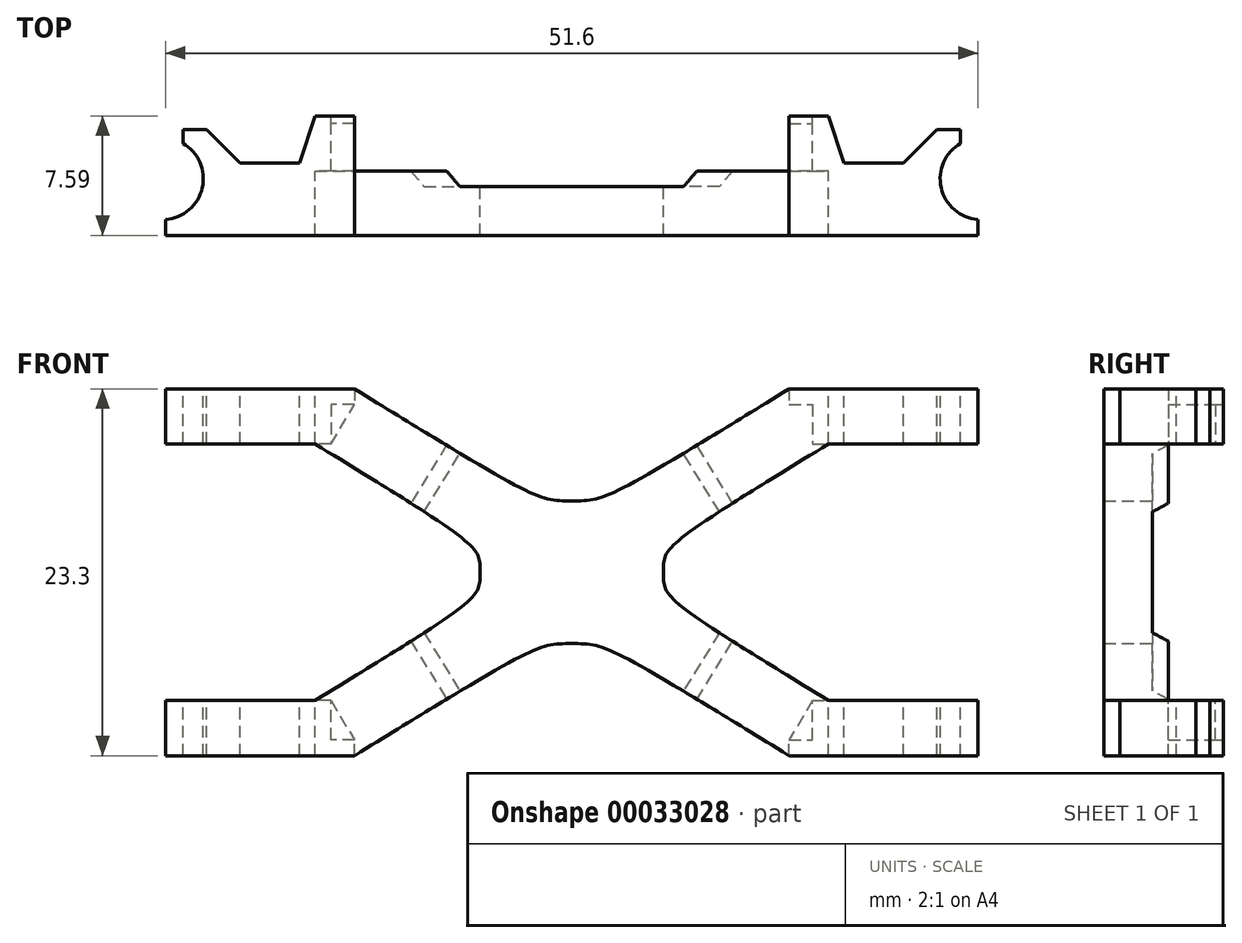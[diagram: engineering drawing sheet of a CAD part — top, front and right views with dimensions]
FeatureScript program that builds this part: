
annotation { "Feature Type Name" : "Feature", "Feature Type Description" : "" }
export const myFeature = defineFeature(function(context is Context, id is Id, definition is map)
    precondition{}
    {
        {
            var Q0;
            Q0=qCreatedBy(makeId("Front.planeOp"),FACE);
            var sketch = newSketch(context, id + "F0", { "sketchPlane" : qUnion([Q0])});
            skLineSegment(sketch, "E0", {"start": v(-15.3, 10.65) * mm, "end": v(-15.3, 8.15) * mm});
            skLineSegment(sketch, "E1", {"start": v(-15.3, 8.15) * mm, "end": v(-16.3, 8.15) * mm});
            skLineSegment(sketch, "E2", {"start": v(-16.3, 8.15) * mm, "end": v(-16.3, 11.65) * mm});
            skLineSegment(sketch, "E3", {"start": v(-16.3, 11.65) * mm, "end": v(-13.8, 11.65) * mm});
            skLineSegment(sketch, "E4", {"start": v(-13.8, 11.65) * mm, "end": v(-13.8, 10.65) * mm});
            skLineSegment(sketch, "E5", {"start": v(-13.8, 10.65) * mm, "end": v(-15.3, 10.65) * mm});
            skLineSegment(sketch, "E6.MirrorCS", {"start": v(13.8, 10.65) * mm, "end": v(15.3, 10.65) * mm});
            skLineSegment(sketch, "E7.MirrorCS", {"start": v(13.8, 11.65) * mm, "end": v(13.8, 10.65) * mm});
            skLineSegment(sketch, "E8.MirrorCS", {"start": v(16.3, 11.65) * mm, "end": v(13.8, 11.65) * mm});
            skLineSegment(sketch, "E9.MirrorCS", {"start": v(16.3, 8.15) * mm, "end": v(16.3, 11.65) * mm});
            skLineSegment(sketch, "E10.MirrorCS", {"start": v(15.3, 10.65) * mm, "end": v(15.3, 8.15) * mm});
            skLineSegment(sketch, "E11.MirrorCS", {"start": v(15.3, 8.15) * mm, "end": v(16.3, 8.15) * mm});
            skLineSegment(sketch, "E12.MirrorCS", {"start": v(15.3, -8.15) * mm, "end": v(16.3, -8.15) * mm});
            skLineSegment(sketch, "E13.MirrorCS", {"start": v(15.3, -10.65) * mm, "end": v(15.3, -8.15) * mm});
            skLineSegment(sketch, "E14.MirrorCS", {"start": v(13.8, -11.65) * mm, "end": v(13.8, -10.65) * mm});
            skLineSegment(sketch, "E15.MirrorCS", {"start": v(16.3, -11.65) * mm, "end": v(13.8, -11.65) * mm});
            skLineSegment(sketch, "E16.MirrorCS", {"start": v(16.3, -8.15) * mm, "end": v(16.3, -11.65) * mm});
            skLineSegment(sketch, "E17.MirrorCS", {"start": v(13.8, -10.65) * mm, "end": v(15.3, -10.65) * mm});
            skLineSegment(sketch, "E18.MirrorCS", {"start": v(-13.8, -11.65) * mm, "end": v(-13.8, -10.65) * mm});
            skLineSegment(sketch, "E19.MirrorCS", {"start": v(-13.8, -10.65) * mm, "end": v(-15.3, -10.65) * mm});
            skLineSegment(sketch, "E20.MirrorCS", {"start": v(-16.3, -11.65) * mm, "end": v(-13.8, -11.65) * mm});
            skLineSegment(sketch, "E21.MirrorCS", {"start": v(-16.3, -8.15) * mm, "end": v(-16.3, -11.65) * mm});
            skLineSegment(sketch, "E22.MirrorCS", {"start": v(-15.3, -8.15) * mm, "end": v(-16.3, -8.15) * mm});
            skLineSegment(sketch, "E23.MirrorCS", {"start": v(-15.3, -10.65) * mm, "end": v(-15.3, -8.15) * mm});
            skSolve(sketch);
        }
        {
            var Q0;
            Q0=qCreatedBy(makeId("Front.planeOp"),FACE);
            var sketch = newSketch(context, id + "F1", { "sketchPlane" : qUnion([Q0])});
            skPoint(sketch, "E24.0", {"position": v(-13.8, 11.65) * mm});
            skPoint(sketch, "E25.0", {"position": v(-16.3, 8.15) * mm});
            skFitSpline(sketch, "E26", {"points": [v(-13.8, 11.65) * mm, v(0, 4.53) * mm], "startDerivative": vector(34.73, -21.35) * mm, "endDerivative": vector(6.67, 0) * mm});
            skFitSpline(sketch, "E27", {"points": [v(-16.3, 8.15) * mm, v(-5.81, 0) * mm], "startDerivative": vector(31.46, -19.34) * mm, "endDerivative": vector(0, -5.11) * mm});
            skFitSpline(sketch, "E28.MirrorCS", {"points": [v(13.8, 11.65) * mm, v(0, 4.53) * mm], "startDerivative": vector(-34.73, -21.35) * mm, "endDerivative": vector(-6.67, 0) * mm});
            skFitSpline(sketch, "E29.MirrorCS", {"points": [v(16.3, 8.15) * mm, v(5.81, 0) * mm], "startDerivative": vector(-31.46, -19.34) * mm, "endDerivative": vector(0, -5.11) * mm});
            skFitSpline(sketch, "E30.MirrorCS", {"points": [v(-16.3, -8.15) * mm, v(-5.81, 0) * mm], "startDerivative": vector(31.46, 19.34) * mm, "endDerivative": vector(0, 5.11) * mm});
            skFitSpline(sketch, "E31.MirrorCS", {"points": [v(-13.8, -11.65) * mm, v(0, -4.53) * mm], "startDerivative": vector(34.73, 21.35) * mm, "endDerivative": vector(6.67, 0) * mm});
            skFitSpline(sketch, "E32.MirrorCS", {"points": [v(13.8, -11.65) * mm, v(0, -4.53) * mm], "startDerivative": vector(-34.73, 21.35) * mm, "endDerivative": vector(-6.67, 0) * mm});
            skFitSpline(sketch, "E33.MirrorCS", {"points": [v(16.3, -8.15) * mm, v(5.81, 0) * mm], "startDerivative": vector(-31.46, 19.34) * mm, "endDerivative": vector(0, 5.11) * mm});
            skLineSegment(sketch, "E34", {"start": v(-13.8, 11.65) * mm, "end": v(-27.96, 11.65) * mm});
            skLineSegment(sketch, "E35", {"start": v(-27.96, 11.65) * mm, "end": v(-27.96, 8.15) * mm});
            skLineSegment(sketch, "E36", {"start": v(-27.96, 8.15) * mm, "end": v(-16.3, 8.15) * mm});
            skLineSegment(sketch, "E37.MirrorCS", {"start": v(27.96, 11.65) * mm, "end": v(27.96, 8.15) * mm});
            skLineSegment(sketch, "E38.MirrorCS", {"start": v(27.96, 8.15) * mm, "end": v(16.3, 8.15) * mm});
            skLineSegment(sketch, "E39.MirrorCS", {"start": v(13.8, 11.65) * mm, "end": v(27.96, 11.65) * mm});
            skLineSegment(sketch, "E40.MirrorCS", {"start": v(27.96, -8.15) * mm, "end": v(16.3, -8.15) * mm});
            skLineSegment(sketch, "E41.MirrorCS", {"start": v(27.96, -11.65) * mm, "end": v(27.96, -8.15) * mm});
            skLineSegment(sketch, "E42.MirrorCS", {"start": v(13.8, -11.65) * mm, "end": v(27.96, -11.65) * mm});
            skLineSegment(sketch, "E43.MirrorCS", {"start": v(-27.96, -8.15) * mm, "end": v(-16.3, -8.15) * mm});
            skLineSegment(sketch, "E44.MirrorCS", {"start": v(-13.8, -11.65) * mm, "end": v(-27.96, -11.65) * mm});
            skLineSegment(sketch, "E45.MirrorCS", {"start": v(-27.96, -11.65) * mm, "end": v(-27.96, -8.15) * mm});
            skLineSegment(sketch, "E46.0", {"start": v(-13.8, -11.65) * mm, "end": v(-13.8, -10.65) * mm});
            skLineSegment(sketch, "E47.0", {"start": v(-13.8, -10.65) * mm, "end": v(-15.3, -10.65) * mm});
            skLineSegment(sketch, "E48.0", {"start": v(-15.3, -10.65) * mm, "end": v(-15.3, -8.15) * mm});
            skLineSegment(sketch, "E49.0", {"start": v(-15.3, -8.15) * mm, "end": v(-16.3, -8.15) * mm});
            skLineSegment(sketch, "E50.0", {"start": v(13.8, -11.65) * mm, "end": v(13.8, -10.65) * mm});
            skLineSegment(sketch, "E51.0", {"start": v(13.8, -10.65) * mm, "end": v(15.3, -10.65) * mm});
            skLineSegment(sketch, "E52.0", {"start": v(15.3, -10.65) * mm, "end": v(15.3, -8.15) * mm});
            skLineSegment(sketch, "E53.0", {"start": v(15.3, -8.15) * mm, "end": v(16.3, -8.15) * mm});
            skLineSegment(sketch, "E54.0", {"start": v(15.3, 8.15) * mm, "end": v(16.3, 8.15) * mm});
            skLineSegment(sketch, "E55.0", {"start": v(15.3, 10.65) * mm, "end": v(15.3, 8.15) * mm});
            skLineSegment(sketch, "E56.0", {"start": v(13.8, 10.65) * mm, "end": v(15.3, 10.65) * mm});
            skLineSegment(sketch, "E57.0", {"start": v(13.8, 11.65) * mm, "end": v(13.8, 10.65) * mm});
            skLineSegment(sketch, "E58.0", {"start": v(-13.8, 11.65) * mm, "end": v(-13.8, 10.65) * mm});
            skLineSegment(sketch, "E59.0", {"start": v(-13.8, 10.65) * mm, "end": v(-15.3, 10.65) * mm});
            skLineSegment(sketch, "E60.0", {"start": v(-15.3, 10.65) * mm, "end": v(-15.3, 8.15) * mm});
            skLineSegment(sketch, "E61.0", {"start": v(-15.3, 8.15) * mm, "end": v(-16.3, 8.15) * mm});
            skLineSegment(sketch, "E62", {"start": v(-15.3, 8.15) * mm, "end": v(-13.8, 10.65) * mm});
            skLineSegment(sketch, "E63", {"start": v(13.8, 10.65) * mm, "end": v(15.3, 8.15) * mm});
            skLineSegment(sketch, "E64", {"start": v(15.3, -8.15) * mm, "end": v(13.8, -10.65) * mm});
            skLineSegment(sketch, "E65", {"start": v(-15.3, -8.15) * mm, "end": v(-13.8, -10.65) * mm});
            skLineSegment(sketch, "E66", {"start": v(-13.8, 11.65) * mm, "end": v(-2.22, 4.53) * mm, "construction": true});
            skLineSegment(sketch, "E67", {"start": v(-5.81, 1.7) * mm, "end": v(-16.3, 8.15) * mm, "construction": true});
            skLineSegment(sketch, "E68", {"start": v(-9.37, 3.85) * mm, "end": v(-7.1, 7.55) * mm});
            skLineSegment(sketch, "E69.MirrorCS", {"start": v(9.37, 3.85) * mm, "end": v(7.1, 7.55) * mm});
            skLineSegment(sketch, "E70.MirrorCS", {"start": v(-9.37, -3.85) * mm, "end": v(-7.1, -7.55) * mm});
            skLineSegment(sketch, "E71.MirrorCS", {"start": v(9.37, -3.85) * mm, "end": v(7.1, -7.55) * mm});
            skSolve(sketch);
        }
        {
            var Q0;
            Q0=qCreatedBy(makeId("Top.planeOp"),FACE);
            var sketch = newSketch(context, id + "F2", { "sketchPlane" : qUnion([Q0])});
            skCircle(sketch, "E72", {"center": v(-26, -4) * mm, "radius": 2.5 * mm, "construction": true});
            skLineSegment(sketch, "E73", {"start": v(0, 0) * mm, "end": v(-16.3, 0) * mm});
            skArc(sketch, "E74", {"start": v(-25.8, -6.6) * mm, "mid": v(-23.46, -4.58) * mm, "end": v(-24.7, -1.75) * mm});
            skLineSegment(sketch, "E75", {"start": v(-25.8, -7.6) * mm, "end": v(-25.8, -6.6) * mm});
            skLineSegment(sketch, "E76", {"start": v(-24.7, -1.75) * mm, "end": v(-22.46, -3.04) * mm, "construction": true});
            skLineSegment(sketch, "E77", {"start": v(-24.7, -0.87) * mm, "end": v(-24.7, -1.75) * mm});
            skLineSegment(sketch, "E78", {"start": v(-25.8, -7.6) * mm, "end": v(0, -7.6) * mm});
            skLineSegment(sketch, "E79.MirrorCS", {"start": v(0, 0) * mm, "end": v(16.3, 0) * mm});
            skLineSegment(sketch, "E80.MirrorCS", {"start": v(25.8, -7.6) * mm, "end": v(0, -7.6) * mm});
            skLineSegment(sketch, "E81.MirrorCS", {"start": v(25.8, -7.6) * mm, "end": v(25.8, -6.6) * mm});
            skArc(sketch, "E82.MirrorCS", {"start": v(25.8, -6.6) * mm, "mid": v(23.46, -4.58) * mm, "end": v(24.7, -1.75) * mm});
            skLineSegment(sketch, "E83.MirrorCS", {"start": v(24.7, -0.87) * mm, "end": v(24.7, -1.75) * mm});
            skPoint(sketch, "E84.0", {"position": v(-16.3, 0) * mm});
            skLineSegment(sketch, "E85", {"start": v(-24.7, -0.87) * mm, "end": v(-23.2, -0.87) * mm});
            skLineSegment(sketch, "E86", {"start": v(-17.3, -3) * mm, "end": v(-16.3, 0) * mm});
            skPoint(sketch, "E87.orphan", {"position": v(-24.7, 0) * mm});
            skLineSegment(sketch, "E88.MirrorCS", {"start": v(24.7, -0.87) * mm, "end": v(23.2, -0.87) * mm});
            skLineSegment(sketch, "E89.MirrorCS", {"start": v(17.3, -3) * mm, "end": v(16.3, 0) * mm});
            skPoint(sketch, "E90.orphan", {"position": v(24.7, 0) * mm});
            skLineSegment(sketch, "E91", {"start": v(-23.2, -0.87) * mm, "end": v(-21.07, -3) * mm});
            skLineSegment(sketch, "E92", {"start": v(-21.07, -3) * mm, "end": v(-17.3, -3) * mm});
            skLineSegment(sketch, "E93.MirrorCS", {"start": v(23.2, -0.87) * mm, "end": v(21.07, -3) * mm});
            skLineSegment(sketch, "E94.MirrorCS", {"start": v(21.07, -3) * mm, "end": v(17.3, -3) * mm});
            skSolve(sketch);
        }
        {
            var Q0;
            Q0=makeQuery(id+"F1.imprint","IMPRINT",FACE,{"disambiguationData":[TD([[makeQuery(id+"F1.imprint","IMPRINT",EDGE,{"derivedFrom":sQuery(id+"F1.wireOp",EDGE,"E34")}),1.0]])]});
            var Q1;
            Q1=makeQuery(id+"F1.imprint","IMPRINT",FACE,{"disambiguationData":[TD([[makeQuery(id+"F1.imprint","IMPRINT",EDGE,{"derivedFrom":sQuery(id+"F1.wireOp",EDGE,"E59.0")}),1.0]])]});
            var Q2;
            {var subQ2=sQuery(id+"F1.wireOp",EDGE,"E58.0");Q2=makeQuery(id+"F1.imprint","IMPRINT",FACE,{"disambiguationData":[TD([[makeQuery(id+"F1.imprint","IMPRINT",EDGE,{"derivedFrom":subQ2}),1.0]])]});}
            var Q3;
            {var subQ2=sQuery(id+"F1.wireOp",EDGE,"E68");Q3=makeQuery(id+"F1.imprint","IMPRINT",FACE,{"disambiguationData":[TD([[makeQuery(id+"F1.imprint","IMPRINT",EDGE,{"derivedFrom":subQ2}),-1.0]])]});}
            var Q4;
            {var subQ2=sQuery(id+"F1.wireOp",EDGE,"E46.0");Q4=makeQuery(id+"F1.imprint","IMPRINT",FACE,{"disambiguationData":[TD([[makeQuery(id+"F1.imprint","IMPRINT",EDGE,{"derivedFrom":subQ2}),-1.0]])]});}
            var Q5;
            Q5=makeQuery(id+"F1.imprint","IMPRINT",FACE,{"disambiguationData":[TD([[makeQuery(id+"F1.imprint","IMPRINT",EDGE,{"derivedFrom":sQuery(id+"F1.wireOp",EDGE,"E47.0")}),-1.0]])]});
            var Q6;
            Q6=makeQuery(id+"F1.imprint","IMPRINT",FACE,{"disambiguationData":[TD([[makeQuery(id+"F1.imprint","IMPRINT",EDGE,{"derivedFrom":sQuery(id+"F1.wireOp",EDGE,"E43.MirrorCS")}),-1.0]])]});
            var Q7;
            {var subQ2=sQuery(id+"F1.wireOp",EDGE,"E50.0");Q7=makeQuery(id+"F1.imprint","IMPRINT",FACE,{"disambiguationData":[TD([[makeQuery(id+"F1.imprint","IMPRINT",EDGE,{"derivedFrom":subQ2}),1.0]])]});}
            var Q8;
            Q8=makeQuery(id+"F1.imprint","IMPRINT",FACE,{"disambiguationData":[TD([[makeQuery(id+"F1.imprint","IMPRINT",EDGE,{"derivedFrom":sQuery(id+"F1.wireOp",EDGE,"E51.0")}),1.0]])]});
            var Q9;
            Q9=makeQuery(id+"F1.imprint","IMPRINT",FACE,{"disambiguationData":[TD([[makeQuery(id+"F1.imprint","IMPRINT",EDGE,{"derivedFrom":sQuery(id+"F1.wireOp",EDGE,"E40.MirrorCS")}),1.0]])]});
            var Q10;
            {var subQ1=sQuery(id+"F1.wireOp",EDGE,"E54.0");Q10=makeQuery(id+"F1.imprint","IMPRINT",FACE,{"disambiguationData":[TD([[makeQuery(id+"F1.imprint","IMPRINT",EDGE,{"derivedFrom":subQ1}),-1.0]])]});}
            var Q11;
            Q11=makeQuery(id+"F1.imprint","IMPRINT",FACE,{"disambiguationData":[TD([[makeQuery(id+"F1.imprint","IMPRINT",EDGE,{"derivedFrom":sQuery(id+"F1.wireOp",EDGE,"E37.MirrorCS")}),-1.0]])]});
            var Q12;
            Q12=makeQuery(id+"F1.imprint","IMPRINT",FACE,{"disambiguationData":[TD([[makeQuery(id+"F1.imprint","IMPRINT",EDGE,{"derivedFrom":sQuery(id+"F1.wireOp",EDGE,"E55.0")}),-1.0]])]});
            extrude(context, id + "F3", {"entities" : qUnion([Q0, Q1, Q2, Q3, Q4, Q5, Q6, Q7, Q8, Q9, Q10, Q11, Q12]), "depth" : 25 * mm});
        }
        {
            var Q0;
            Q0=makeQuery(id+"F2.imprint","IMPRINT",FACE,{"disambiguationData":[TD([[makeQuery(id+"F2.imprint","IMPRINT",EDGE,{"derivedFrom":sQuery(id+"F2.wireOp",EDGE,"E73")}),1.0]])]});
            extrude(context, id + "F4", {"entities" : qUnion([Q0]), "operationType" : NewBodyOperationType.INTERSECT, "endBound" : BoundingType.SYMMETRIC, "oppositeDirection" : true, "depth" : 30 * mm});
        }
        {
            var Q0;
            Q0=makeQuery(id+"F1.imprint","IMPRINT",FACE,{"disambiguationData":[TD([[makeQuery(id+"F1.imprint","IMPRINT",EDGE,{"derivedFrom":sQuery(id+"F1.wireOp",EDGE,"E26")}),-1.0]])]});
            var Q1;
            {var subQ2=sQuery(id+"F1.wireOp",EDGE,"E68");Q1=makeQuery(id+"F1.imprint","IMPRINT",FACE,{"disambiguationData":[TD([[makeQuery(id+"F1.imprint","IMPRINT",EDGE,{"derivedFrom":subQ2}),-1.0]])]});}
            var Q2;
            {var subQ2=sQuery(id+"F1.wireOp",EDGE,"E46.0");Q2=makeQuery(id+"F1.imprint","IMPRINT",FACE,{"disambiguationData":[TD([[makeQuery(id+"F1.imprint","IMPRINT",EDGE,{"derivedFrom":subQ2}),-1.0]])]});}
            var Q3;
            {var subQ2=sQuery(id+"F1.wireOp",EDGE,"E50.0");Q3=makeQuery(id+"F1.imprint","IMPRINT",FACE,{"disambiguationData":[TD([[makeQuery(id+"F1.imprint","IMPRINT",EDGE,{"derivedFrom":subQ2}),1.0]])]});}
            var Q4;
            {var subQ1=sQuery(id+"F1.wireOp",EDGE,"E54.0");Q4=makeQuery(id+"F1.imprint","IMPRINT",FACE,{"disambiguationData":[TD([[makeQuery(id+"F1.imprint","IMPRINT",EDGE,{"derivedFrom":subQ1}),-1.0]])]});}
            var Q5;
            Q5=makeQuery(id+"F1.imprint","IMPRINT",FACE,{"disambiguationData":[TD([[makeQuery(id+"F1.imprint","IMPRINT",EDGE,{"derivedFrom":sQuery(id+"F1.wireOp",EDGE,"E59.0")}),1.0]])]});
            var Q6;
            Q6=makeQuery(id+"F1.imprint","IMPRINT",FACE,{"disambiguationData":[TD([[makeQuery(id+"F1.imprint","IMPRINT",EDGE,{"derivedFrom":sQuery(id+"F1.wireOp",EDGE,"E47.0")}),-1.0]])]});
            var Q7;
            Q7=makeQuery(id+"F1.imprint","IMPRINT",FACE,{"disambiguationData":[TD([[makeQuery(id+"F1.imprint","IMPRINT",EDGE,{"derivedFrom":sQuery(id+"F1.wireOp",EDGE,"E51.0")}),1.0]])]});
            var Q8;
            Q8=makeQuery(id+"F1.imprint","IMPRINT",FACE,{"disambiguationData":[TD([[makeQuery(id+"F1.imprint","IMPRINT",EDGE,{"derivedFrom":sQuery(id+"F1.wireOp",EDGE,"E55.0")}),-1.0]])]});
            extrude(context, id + "F5", {"entities" : qUnion([Q0, Q1, Q2, Q3, Q4, Q5, Q6, Q7, Q8]), "operationType" : NewBodyOperationType.REMOVE, "depth" : 3.5 * mm});
        }
        {
            var Q0;
            {var subQ2=sQuery(id+"F1.wireOp",EDGE,"E68");Q0=makeQuery(id+"F1.imprint","IMPRINT",FACE,{"disambiguationData":[TD([[makeQuery(id+"F1.imprint","IMPRINT",EDGE,{"derivedFrom":subQ2}),-1.0]])]});}
            extrude(context, id + "F6", {"entities" : qUnion([Q0]), "operationType" : NewBodyOperationType.REMOVE, "depth" : 4.5 * mm});
        }
        {
            var Q0;
            Q0=makeQuery(id+"F6.boolean.opBoolean","INTERSECT",EDGE,{"derivedFrom":[makeQuery(id+"F5.boolean.opBoolean","COPY",FACE,{"derivedFrom":makeQuery(id+"F5.opExtrude","CAP_FACE",FACE,{"disambiguationData":[OSD([sQuery(id+"F1.wireOp",EDGE,"E26"),sQuery(id+"F1.wireOp",EDGE,"E27"),sQuery(id+"F1.wireOp",EDGE,"E28.MirrorCS"),sQuery(id+"F1.wireOp",EDGE,"E29.MirrorCS"),sQuery(id+"F1.wireOp",EDGE,"E30.MirrorCS"),sQuery(id+"F1.wireOp",EDGE,"E31.MirrorCS"),sQuery(id+"F1.wireOp",EDGE,"E32.MirrorCS"),sQuery(id+"F1.wireOp",EDGE,"E33.MirrorCS"),sQuery(id+"F1.wireOp",EDGE,"E46.0"),sQuery(id+"F1.wireOp",EDGE,"E47.0"),sQuery(id+"F1.wireOp",EDGE,"E48.0"),sQuery(id+"F1.wireOp",EDGE,"E49.0"),sQuery(id+"F1.wireOp",EDGE,"E50.0"),sQuery(id+"F1.wireOp",EDGE,"E51.0"),sQuery(id+"F1.wireOp",EDGE,"E52.0"),sQuery(id+"F1.wireOp",EDGE,"E53.0"),sQuery(id+"F1.wireOp",EDGE,"E54.0"),sQuery(id+"F1.wireOp",EDGE,"E55.0"),sQuery(id+"F1.wireOp",EDGE,"E56.0"),sQuery(id+"F1.wireOp",EDGE,"E57.0"),sQuery(id+"F1.wireOp",EDGE,"E58.0"),sQuery(id+"F1.wireOp",EDGE,"E59.0"),sQuery(id+"F1.wireOp",EDGE,"E60.0"),sQuery(id+"F1.wireOp",EDGE,"E61.0")])],"isStart":false})}),makeQuery(id+"F6.opExtrude","SWEPT_FACE",FACE,{"disambiguationData":[OSD([sQuery(id+"F1.wireOp",EDGE,"E69.MirrorCS")])]})]});
            var Q1;
            Q1=makeQuery(id+"F6.boolean.opBoolean","INTERSECT",EDGE,{"derivedFrom":[makeQuery(id+"F5.boolean.opBoolean","COPY",FACE,{"derivedFrom":makeQuery(id+"F5.opExtrude","CAP_FACE",FACE,{"disambiguationData":[OSD([sQuery(id+"F1.wireOp",EDGE,"E26"),sQuery(id+"F1.wireOp",EDGE,"E27"),sQuery(id+"F1.wireOp",EDGE,"E28.MirrorCS"),sQuery(id+"F1.wireOp",EDGE,"E29.MirrorCS"),sQuery(id+"F1.wireOp",EDGE,"E30.MirrorCS"),sQuery(id+"F1.wireOp",EDGE,"E31.MirrorCS"),sQuery(id+"F1.wireOp",EDGE,"E32.MirrorCS"),sQuery(id+"F1.wireOp",EDGE,"E33.MirrorCS"),sQuery(id+"F1.wireOp",EDGE,"E46.0"),sQuery(id+"F1.wireOp",EDGE,"E47.0"),sQuery(id+"F1.wireOp",EDGE,"E48.0"),sQuery(id+"F1.wireOp",EDGE,"E49.0"),sQuery(id+"F1.wireOp",EDGE,"E50.0"),sQuery(id+"F1.wireOp",EDGE,"E51.0"),sQuery(id+"F1.wireOp",EDGE,"E52.0"),sQuery(id+"F1.wireOp",EDGE,"E53.0"),sQuery(id+"F1.wireOp",EDGE,"E54.0"),sQuery(id+"F1.wireOp",EDGE,"E55.0"),sQuery(id+"F1.wireOp",EDGE,"E56.0"),sQuery(id+"F1.wireOp",EDGE,"E57.0"),sQuery(id+"F1.wireOp",EDGE,"E58.0"),sQuery(id+"F1.wireOp",EDGE,"E59.0"),sQuery(id+"F1.wireOp",EDGE,"E60.0"),sQuery(id+"F1.wireOp",EDGE,"E61.0")])],"isStart":false})}),makeQuery(id+"F6.opExtrude","SWEPT_FACE",FACE,{"disambiguationData":[OSD([sQuery(id+"F1.wireOp",EDGE,"E68")])]})]});
            var Q2;
            Q2=makeQuery(id+"F6.boolean.opBoolean","INTERSECT",EDGE,{"derivedFrom":[makeQuery(id+"F5.boolean.opBoolean","COPY",FACE,{"derivedFrom":makeQuery(id+"F5.opExtrude","CAP_FACE",FACE,{"disambiguationData":[OSD([sQuery(id+"F1.wireOp",EDGE,"E26"),sQuery(id+"F1.wireOp",EDGE,"E27"),sQuery(id+"F1.wireOp",EDGE,"E28.MirrorCS"),sQuery(id+"F1.wireOp",EDGE,"E29.MirrorCS"),sQuery(id+"F1.wireOp",EDGE,"E30.MirrorCS"),sQuery(id+"F1.wireOp",EDGE,"E31.MirrorCS"),sQuery(id+"F1.wireOp",EDGE,"E32.MirrorCS"),sQuery(id+"F1.wireOp",EDGE,"E33.MirrorCS"),sQuery(id+"F1.wireOp",EDGE,"E46.0"),sQuery(id+"F1.wireOp",EDGE,"E47.0"),sQuery(id+"F1.wireOp",EDGE,"E48.0"),sQuery(id+"F1.wireOp",EDGE,"E49.0"),sQuery(id+"F1.wireOp",EDGE,"E50.0"),sQuery(id+"F1.wireOp",EDGE,"E51.0"),sQuery(id+"F1.wireOp",EDGE,"E52.0"),sQuery(id+"F1.wireOp",EDGE,"E53.0"),sQuery(id+"F1.wireOp",EDGE,"E54.0"),sQuery(id+"F1.wireOp",EDGE,"E55.0"),sQuery(id+"F1.wireOp",EDGE,"E56.0"),sQuery(id+"F1.wireOp",EDGE,"E57.0"),sQuery(id+"F1.wireOp",EDGE,"E58.0"),sQuery(id+"F1.wireOp",EDGE,"E59.0"),sQuery(id+"F1.wireOp",EDGE,"E60.0"),sQuery(id+"F1.wireOp",EDGE,"E61.0")])],"isStart":false})}),makeQuery(id+"F6.opExtrude","SWEPT_FACE",FACE,{"disambiguationData":[OSD([sQuery(id+"F1.wireOp",EDGE,"E70.MirrorCS")])]})]});
            var Q3;
            Q3=makeQuery(id+"F6.boolean.opBoolean","INTERSECT",EDGE,{"derivedFrom":[makeQuery(id+"F5.boolean.opBoolean","COPY",FACE,{"derivedFrom":makeQuery(id+"F5.opExtrude","CAP_FACE",FACE,{"disambiguationData":[OSD([sQuery(id+"F1.wireOp",EDGE,"E26"),sQuery(id+"F1.wireOp",EDGE,"E27"),sQuery(id+"F1.wireOp",EDGE,"E28.MirrorCS"),sQuery(id+"F1.wireOp",EDGE,"E29.MirrorCS"),sQuery(id+"F1.wireOp",EDGE,"E30.MirrorCS"),sQuery(id+"F1.wireOp",EDGE,"E31.MirrorCS"),sQuery(id+"F1.wireOp",EDGE,"E32.MirrorCS"),sQuery(id+"F1.wireOp",EDGE,"E33.MirrorCS"),sQuery(id+"F1.wireOp",EDGE,"E46.0"),sQuery(id+"F1.wireOp",EDGE,"E47.0"),sQuery(id+"F1.wireOp",EDGE,"E48.0"),sQuery(id+"F1.wireOp",EDGE,"E49.0"),sQuery(id+"F1.wireOp",EDGE,"E50.0"),sQuery(id+"F1.wireOp",EDGE,"E51.0"),sQuery(id+"F1.wireOp",EDGE,"E52.0"),sQuery(id+"F1.wireOp",EDGE,"E53.0"),sQuery(id+"F1.wireOp",EDGE,"E54.0"),sQuery(id+"F1.wireOp",EDGE,"E55.0"),sQuery(id+"F1.wireOp",EDGE,"E56.0"),sQuery(id+"F1.wireOp",EDGE,"E57.0"),sQuery(id+"F1.wireOp",EDGE,"E58.0"),sQuery(id+"F1.wireOp",EDGE,"E59.0"),sQuery(id+"F1.wireOp",EDGE,"E60.0"),sQuery(id+"F1.wireOp",EDGE,"E61.0")])],"isStart":false})}),makeQuery(id+"F6.opExtrude","SWEPT_FACE",FACE,{"disambiguationData":[OSD([sQuery(id+"F1.wireOp",EDGE,"E71.MirrorCS")])]})]});
            chamfer(context, id + "F7", {"entities" : qUnion([Q0, Q1, Q2, Q3]), "width" : 1 * mm, "tangentPropagation" : true});
        }
        {
            var Q0;
            Q0=makeQuery(id+"F1.imprint","IMPRINT",FACE,{"disambiguationData":[TD([[makeQuery(id+"F1.imprint","IMPRINT",EDGE,{"derivedFrom":sQuery(id+"F1.wireOp",EDGE,"E51.0")}),1.0]])]});
            var Q1;
            Q1=makeQuery(id+"F1.imprint","IMPRINT",FACE,{"disambiguationData":[TD([[makeQuery(id+"F1.imprint","IMPRINT",EDGE,{"derivedFrom":sQuery(id+"F1.wireOp",EDGE,"E47.0")}),-1.0]])]});
            var Q2;
            Q2=makeQuery(id+"F1.imprint","IMPRINT",FACE,{"disambiguationData":[TD([[makeQuery(id+"F1.imprint","IMPRINT",EDGE,{"derivedFrom":sQuery(id+"F1.wireOp",EDGE,"E59.0")}),1.0]])]});
            extrude(context, id + "F8", {"entities" : qUnion([Q0, Q1, Q2]), "operationType" : NewBodyOperationType.ADD, "depth" : 0.5 * mm});
        }
    });
